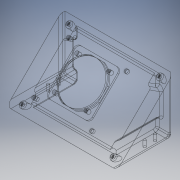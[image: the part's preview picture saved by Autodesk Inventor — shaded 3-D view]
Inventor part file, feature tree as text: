
AUTODESK INVENTOR PART (.ipt)
format: ipt  version: 2019 (Build 230136000, 136)  size: 277,504 bytes
history: native  units: in
note: dims shown in document units (in); Inventor stores cm internally (conversion verified against a paired STEP export)
features: other x1, extrude x1, sketch x1, imported_body x1
ambient origin geometry x8: Origin, YZ Plane, XZ Plane, XY Plane, X Axis, Y Axis, Z Axis, Center Point
bodies: Body1 (feature_tree)
feature tree (4):
  other  "實體1"
  extrude  "擠出1"  Depth=0.0984in
  sketch  "草圖1"
  imported_body  "Base1"
